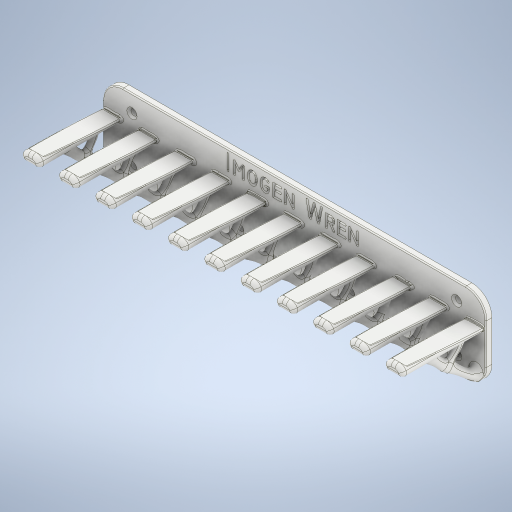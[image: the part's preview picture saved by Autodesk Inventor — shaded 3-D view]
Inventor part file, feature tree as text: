
AUTODESK INVENTOR PART (.ipt)
format: ipt  version: 2023 (Build 270158030, 158C)  size: 3,738,112 bytes
history: native  units: mm
features: fillet x2, hole x1, extrude x1, sketch x1
ambient origin geometry x8: Origin, YZ Plane, XZ Plane, XY Plane, X Axis, Y Axis, Z Axis, Center Point
bodies: Solid1 (feature_tree), Body80 (feature_tree)
feature tree (5):
  fillet  "Fillet1"  Radius=10.0mm
  fillet  "Fillet2"  Radius=0.5mm
  hole  "Hole1"  [1 undecoded]
  extrude  "Extrusion1"  Depth=8.0mm
  sketch  "Sketch3"  dims[d5=5.0mm d6=8.0mm d7=8.0mm d8=14.0mm d9=14.0mm d10=3.0mm d11=10.0mm d12=5.0mm d13=1.0mm d14=90.0deg d15=8.0mm d16=20.594885mm d94=2.5mm d95=0.0mm]
note: 1 required parameter value undecoded (feature->parameter linkage not recoverable at this tier; creation-order binding heuristic only, values carry confidence <= 0.55)
